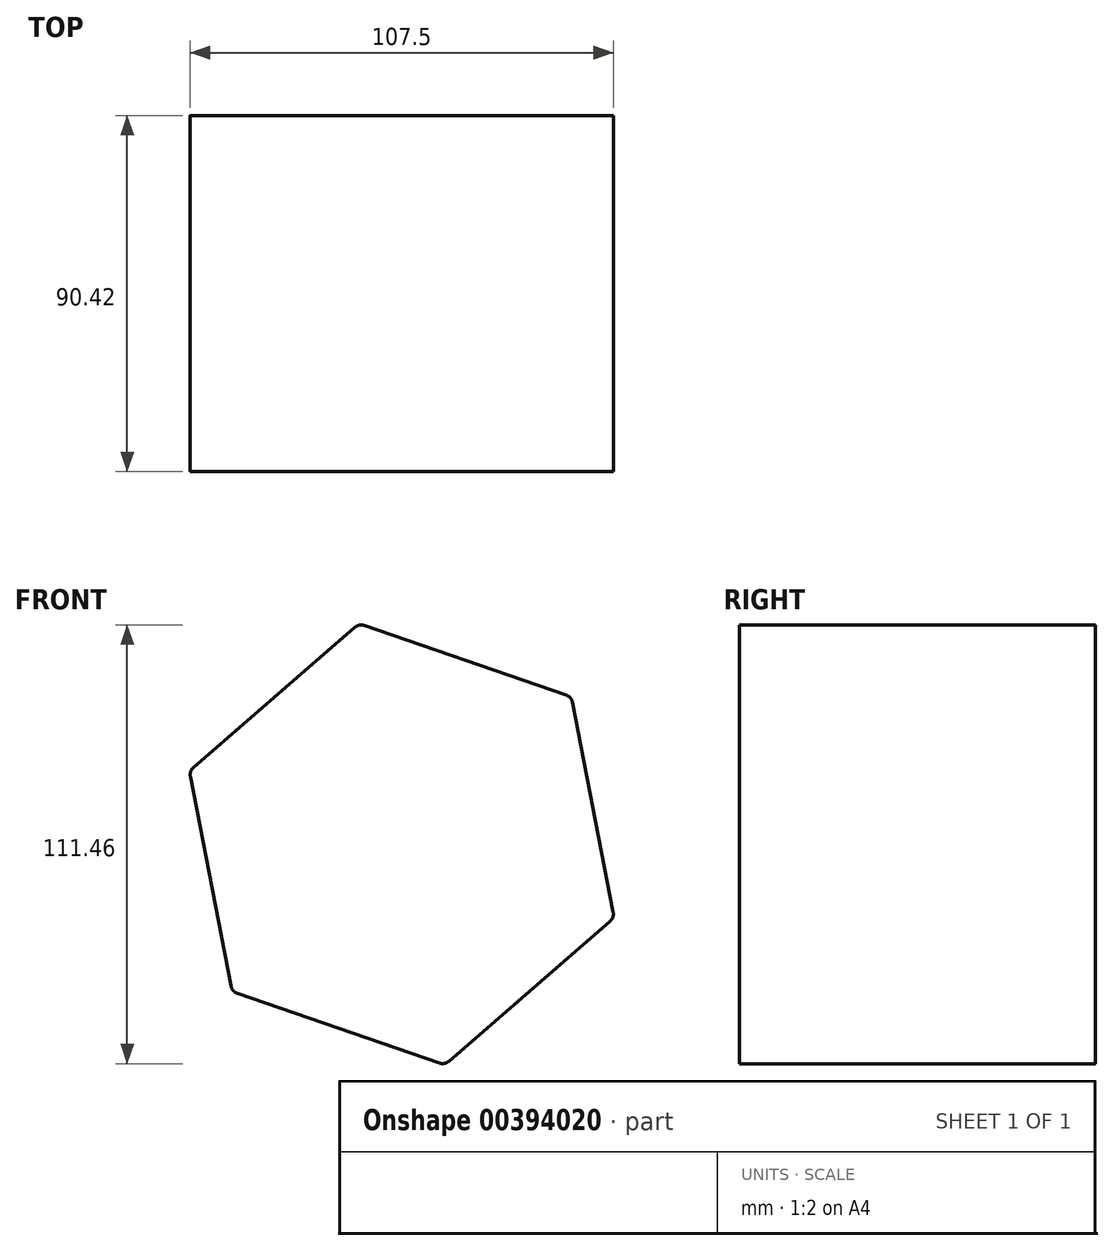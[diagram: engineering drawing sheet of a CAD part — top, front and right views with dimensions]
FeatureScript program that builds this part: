
annotation { "Feature Type Name" : "Feature", "Feature Type Description" : "" }
export const myFeature = defineFeature(function(context is Context, id is Id, definition is map)
    precondition{}
    {
        {
            var Q0;
            Q0=qCreatedBy(makeId("Front.planeOp"),FACE);
            var sketch = newSketch(context, id + "F0", { "sketchPlane" : qUnion([Q0])});
            skCircle(sketch, "E0.cCircle", {"center": v(0, 0) * mm, "radius": 49.44 * mm, "construction": true});
            skLineSegment(sketch, "E0.0", {"start": v(43.1, 37.43) * mm, "end": v(53.97, -18.6) * mm});
            skLineSegment(sketch, "E0.1", {"start": v(53.97, -18.6) * mm, "end": v(10.87, -56.04) * mm});
            skLineSegment(sketch, "E0.2", {"start": v(10.87, -56.04) * mm, "end": v(-43.1, -37.43) * mm});
            skLineSegment(sketch, "E0.3", {"start": v(-43.1, -37.43) * mm, "end": v(-53.97, 18.6) * mm});
            skLineSegment(sketch, "E0.4", {"start": v(-53.97, 18.6) * mm, "end": v(-10.87, 56.04) * mm});
            skLineSegment(sketch, "E0.5", {"start": v(-10.87, 56.04) * mm, "end": v(43.1, 37.43) * mm});
            skPoint(sketch, "E0.0.midPoint", {"position": v(48.54, 9.41) * mm});
            skSolve(sketch);
        }
        {
            var Q0;
            Q0=makeQuery(id+"F0.imprint","IMPRINT",FACE,{"disambiguationData":[TD([[makeQuery(id+"F0.imprint","IMPRINT",EDGE,{"derivedFrom":sQuery(id+"F0.wireOp",EDGE,"E0.0")}),-1.0]])]});
            var Q1;
            Q1=sQuery(id+"F0.wireOp",EDGE,"E0.5");
            var Q2;
            Q2=sQuery(id+"F0.wireOp",EDGE,"E0.4");
            var Q3;
            Q3=sQuery(id+"F0.wireOp",EDGE,"E0.3");
            var Q4;
            Q4=sQuery(id+"F0.wireOp",EDGE,"E0.2");
            var Q5;
            Q5=sQuery(id+"F0.wireOp",EDGE,"E0.1");
            var Q6;
            Q6=sQuery(id+"F0.wireOp",EDGE,"E0.0");
            extrude(context, id + "F1", {"entities" : qUnion([Q0]), "surfaceEntities" : qUnion([Q1, Q2, Q3, Q4, Q5, Q6]), "endBound" : BoundingType.SYMMETRIC, "depth" : 90.42 * mm});
        }
        {
            var Q0;
            Q0=makeQuery(id+"F1.opExtrude","SWEPT_EDGE",EDGE,{"disambiguationData":[OSD([sQuery(id+"F0.wireOp",EDGE,"E0.4"),sQuery(id+"F0.wireOp",EDGE,"E0.5")])]});
            var Q1;
            Q1=makeQuery(id+"F1.opExtrude","SWEPT_EDGE",EDGE,{"disambiguationData":[OSD([sQuery(id+"F0.wireOp",EDGE,"E0.0"),sQuery(id+"F0.wireOp",EDGE,"E0.5")])]});
            var Q2;
            Q2=makeQuery(id+"F1.opExtrude","SWEPT_EDGE",EDGE,{"disambiguationData":[OSD([sQuery(id+"F0.wireOp",EDGE,"E0.3"),sQuery(id+"F0.wireOp",EDGE,"E0.4")])]});
            var Q3;
            Q3=makeQuery(id+"F1.opExtrude","SWEPT_EDGE",EDGE,{"disambiguationData":[OSD([sQuery(id+"F0.wireOp",EDGE,"E0.2"),sQuery(id+"F0.wireOp",EDGE,"E0.3")])]});
            var Q4;
            Q4=makeQuery(id+"F1.opExtrude","SWEPT_EDGE",EDGE,{"disambiguationData":[OSD([sQuery(id+"F0.wireOp",EDGE,"E0.1"),sQuery(id+"F0.wireOp",EDGE,"E0.2")])]});
            var Q5;
            Q5=makeQuery(id+"F1.opExtrude","SWEPT_EDGE",EDGE,{"disambiguationData":[OSD([sQuery(id+"F0.wireOp",EDGE,"E0.0"),sQuery(id+"F0.wireOp",EDGE,"E0.1")])]});
            fillet(context, id + "F2", {"entities" : qUnion([Q0, Q1, Q2, Q3, Q4, Q5]), "radius" : 2.54 * mm, "tangentPropagation" : true, "rho" : 0.5, "crossSection" : FilletCrossSection.CONIC, "allowEdgeOverflow" : false});
        }
    });
